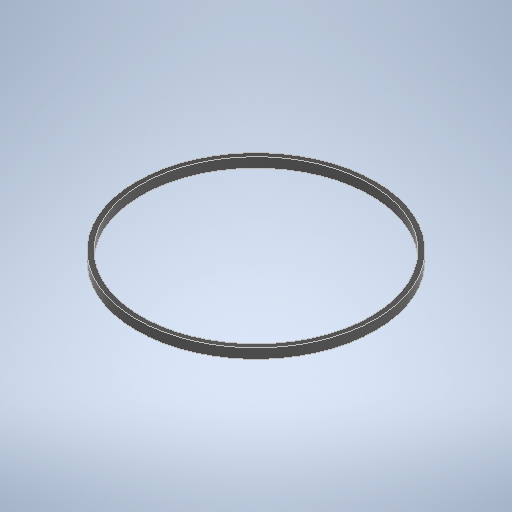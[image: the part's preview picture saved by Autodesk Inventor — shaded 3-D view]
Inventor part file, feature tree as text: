
AUTODESK INVENTOR PART (.ipt)
format: ipt  version: 2025.1 (Build 291241000, 241)  size: 258,048 bytes
history: native  units: mm
features: extrude x1, sketch x1
ambient origin geometry x8: Origin, YZ Plane, XZ Plane, XY Plane, X Axis, Y Axis, Z Axis, Center Point
bodies: Solid1 (feature_tree)
feature tree (2):
  extrude  "Extrusion1"  Depth=1.0mm
  sketch  "Sketch1"  dims[d0=24.0mm d1=23.0mm d2=1.0mm d3=0.0mm]
